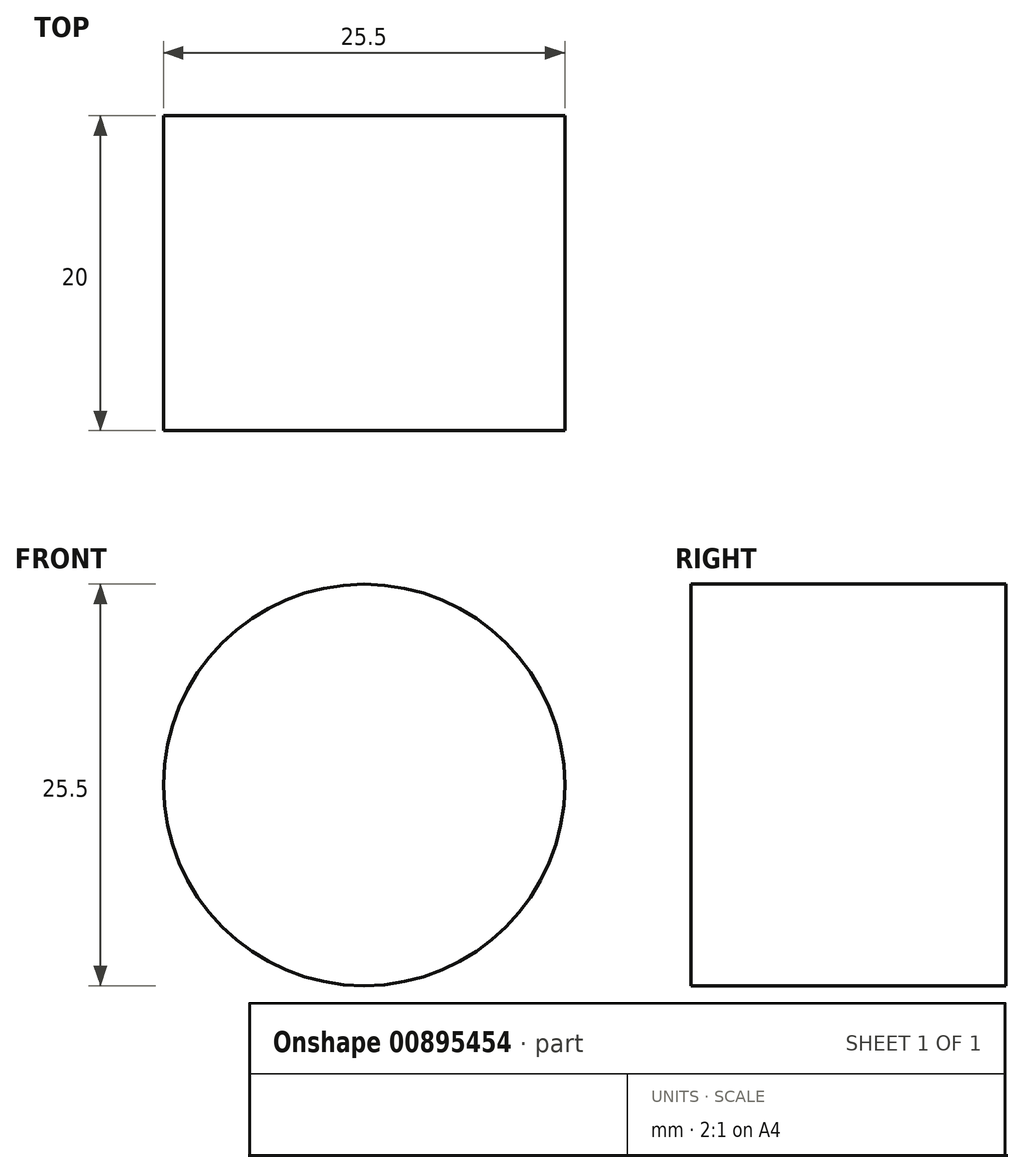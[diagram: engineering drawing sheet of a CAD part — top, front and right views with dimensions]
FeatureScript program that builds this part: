
annotation { "Feature Type Name" : "Feature", "Feature Type Description" : "" }
export const myFeature = defineFeature(function(context is Context, id is Id, definition is map)
    precondition{}
    {
        {
            var Q0;
            Q0=qCreatedBy(makeId("Front.planeOp"),FACE);
            var sketch = newSketch(context, id + "F0", { "sketchPlane" : qUnion([Q0])});
            skCircle(sketch, "E0", {"center": v(0, 0) * mm, "radius": 12.75 * mm});
            skSolve(sketch);
        }
        {
            var Q0;
            Q0=makeQuery(id+"F0.imprint","IMPRINT",FACE,{"disambiguationData":[TD([[makeQuery(id+"F0.imprint","IMPRINT",EDGE,{"derivedFrom":sQuery(id+"F0.wireOp",EDGE,"E0")}),1.0]])]});
            extrude(context, id + "F1", {"entities" : qUnion([Q0]), "oppositeDirection" : true, "depth" : 20 * mm, "offsetDistance" : 25.4 * mm});
        }
    });
